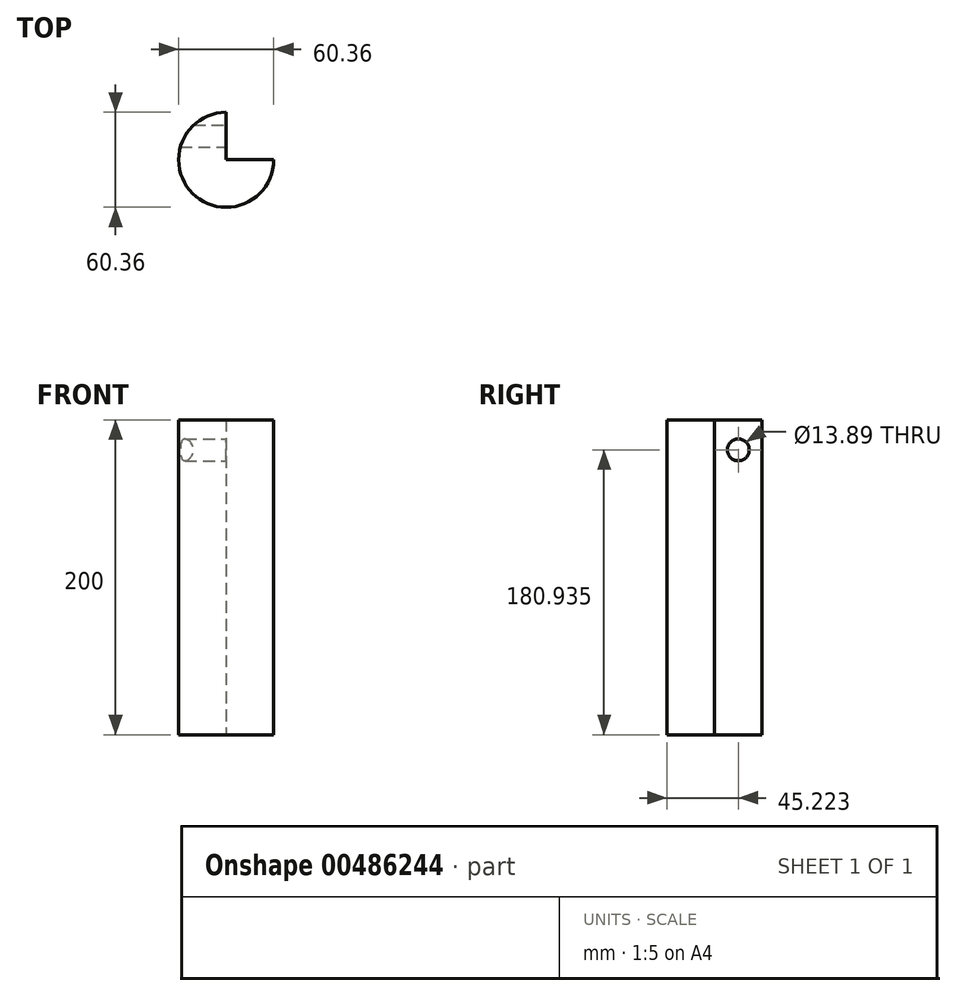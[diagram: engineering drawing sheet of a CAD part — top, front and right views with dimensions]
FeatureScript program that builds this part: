
annotation { "Feature Type Name" : "Feature", "Feature Type Description" : "" }
export const myFeature = defineFeature(function(context is Context, id is Id, definition is map)
    precondition{}
    {
        {
            var Q0;
            Q0=qCreatedBy(makeId("Top.planeOp"),FACE);
            var sketch = newSketch(context, id + "F0", { "sketchPlane" : qUnion([Q0])});
            skCircle(sketch, "E0", {"center": v(0, 0) * mm, "radius": 30.18 * mm});
            skLineSegment(sketch, "E1", {"start": v(0, 0) * mm, "end": v(0, 30.18) * mm});
            skLineSegment(sketch, "E2", {"start": v(0, 0) * mm, "end": v(30.18, 0) * mm});
            skSolve(sketch);
        }
        {
            var Q0;
            {var subQ0=sQuery(id+"F0.wireOp",EDGE,"E1");Q0=makeQuery(id+"F0.imprint","IMPRINT",FACE,{"disambiguationData":[TD([[makeQuery(id+"F0.imprint","IMPRINT",EDGE,{"derivedFrom":subQ0}),1.0]])]});}
            extrude(context, id + "F1", {"entities" : qUnion([Q0]), "depth" : 200 * mm});
        }
        {
            var Q0;
            Q0=makeQuery(id+"F1.opExtrude","SWEPT_FACE",FACE,{"disambiguationData":[OSD([sQuery(id+"F0.wireOp",EDGE,"E1")])]});
            var sketch = newSketch(context, id + "F2", { "sketchPlane" : qUnion([Q0])});
            skCircle(sketch, "E3", {"center": v(15.04, 180.94) * mm, "radius": 6.95 * mm});
            skSolve(sketch);
        }
        {
            var Q0;
            Q0=makeQuery(id+"F2.imprint","IMPRINT",FACE,{"disambiguationData":[TD([[makeQuery(id+"F2.imprint","IMPRINT",EDGE,{"derivedFrom":sQuery(id+"F2.wireOp",EDGE,"E3")}),1.0]])]});
            extrude(context, id + "F3", {"entities" : qUnion([Q0]), "operationType" : NewBodyOperationType.REMOVE, "oppositeDirection" : true, "depth" : 91.31 * mm});
        }
    });
